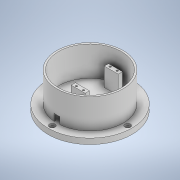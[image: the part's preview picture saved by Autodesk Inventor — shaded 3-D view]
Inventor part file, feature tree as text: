
AUTODESK INVENTOR PART (.ipt)
format: ipt  version: 2022 (Build 260153000, 153)  size: 357,376 bytes
history: native  units: in
note: dims shown in document units (in); Inventor stores cm internally (conversion verified against a paired STEP export)
features: extrude x19, sketch x19, thread x4
ambient origin geometry x8: Origin, YZ Plane, XZ Plane, XY Plane, X Axis, Y Axis, Z Axis, Center Point
bodies: Solid1 (feature_tree)
feature tree (42):
  extrude  "Extrusion1"  Depth=0.315in TaperAngle=0.0deg
  extrude  "Extrusion2"  Depth=0.1969in
  extrude  "Extrusion3"  Depth=0.1969in
  extrude  "Extrusion4"  Depth=0.1969in
  extrude  "Extrusion5"  Depth=0.1969in
  extrude  "Extrusion6"  Depth=0.315in
  extrude  "Extrusion7"  Depth=0.1969in
  extrude  "Extrusion8"  Depth=0.1969in
  extrude  "Extrusion9"  Depth=0.1181in TaperAngle=0.0deg
  extrude  "Extrusion10"  Depth=3.5433in
  extrude  "Extrusion11"  Depth=0.3937in
  extrude  "Extrusion12"  Depth=0.7874in
  thread  "Thread1"  [1 undecoded]
  thread  "Thread2"  [1 undecoded]
  thread  "Thread3"  [1 undecoded]
  thread  "Thread4"  [1 undecoded]
  extrude  "Extrusion13"  Depth=1.5748in
  extrude  "Extrusion14"  Depth=0.315in
  extrude  "Extrusion15"  Depth=0.315in TaperAngle=0.0deg
  extrude  "Extrusion16"  Depth=0.1575in
  extrude  "Extrusion17"  Depth=0.8661in TaperAngle=0.0deg
  extrude  "Extrusion18"  Depth=0.1969in
  extrude  "Extrusion19"  Depth=0.1575in
  sketch  "Sketch1"  dims[d0=4.7244in d1=0.315in d2=0.0in]
  sketch  "Sketch2"  dims[d3=0.315in d4=0.1969in]
  sketch  "Sketch3"  dims[d5=0.315in d6=0.1969in]
  sketch  "Sketch4"  dims[d7=0.315in d8=0.1969in]
  sketch  "Sketch5"  dims[d9=0.315in d10=0.1969in]
  sketch  "Sketch6"  dims[d11=0.315in d12=0.0in d13=0.315in]
  sketch  "Sketch7"  dims[d14=0.315in d15=0.1969in]
  sketch  "Sketch8"  dims[d16=0.315in d17=0.1969in]
  sketch  "Sketch9"  dims[d18=0.315in d19=0.1181in d20=0.0in]
  sketch  "Sketch10"  dims[d21=3.7402in d22=3.5433in]
  sketch  "Sketch11"  dims[d23=0.3937in d24=0.3543in]
  sketch  "Sketch12"  dims[d25=0.3937in d26=0.2756in d27=0.3937in d28=0.0in d29=0.3937in d30=0.3543in d31=0.7874in]
  sketch  "Sketch13"  dims[d32=0.2756in d33=1.5748in]
  sketch  "Sketch14"  dims[d34=0.315in d35=0.315in]
  sketch  "Sketch16"  dims[d36=0.315in d37=1.1024in d38=0.0in]
  sketch  "Sketch17"  dims[d39=0.1575in d40=0.1575in]
  sketch  "Sketch18"  dims[d41=1.1024in d42=0.0in d43=0.8661in d44=0.0in]
  sketch  "Sketch19"  dims[d45=0.0787in d46=0.1969in]
  sketch  "Sketch20"  dims[d47=0.1969in d48=0.1575in d49=0.1575in d50=0.0787in d51=0.1575in d52=0.1575in d53=0.3937in d54=0.0in d55=1.1024in d56=0.0in d57=0.3937in d58=1.437in d59=0.6654in d60=0.3937in d61=0.2362in d62=0.2362in d63=0.2362in d64=0.2362in d65=0.3937in d66=0.0in d67=0.6575in d68=0.0in d69=0.1004in d70=0.1004in d71=0.1988in d72=0.1988in d73=0.1988in d74=0.1988in d75=0.1063in d76=0.1063in d77=0.1063in d78=0.1063in d79=0.3937in d80=0.0in d81=0.3937in d82=0.0in d83=0.3937in d84=0.0in d85=0.3937in d86=0.0in d87=0.3937in d88=0.0in d89=1.8622in d90=0.0in d91=1.6732in d92=0.0in d93=1.6732in d94=0.0in d95=0.315in d96=0.0in d97=3.7402in d98=3.5433in d99=1.6732in d100=0.0in d101=2.0187in d102=0.0in d103=3.2313in d104=0.0in]
note: 4 required parameter values undecoded (feature->parameter linkage not recoverable at this tier; creation-order binding heuristic only, values carry confidence <= 0.55)
